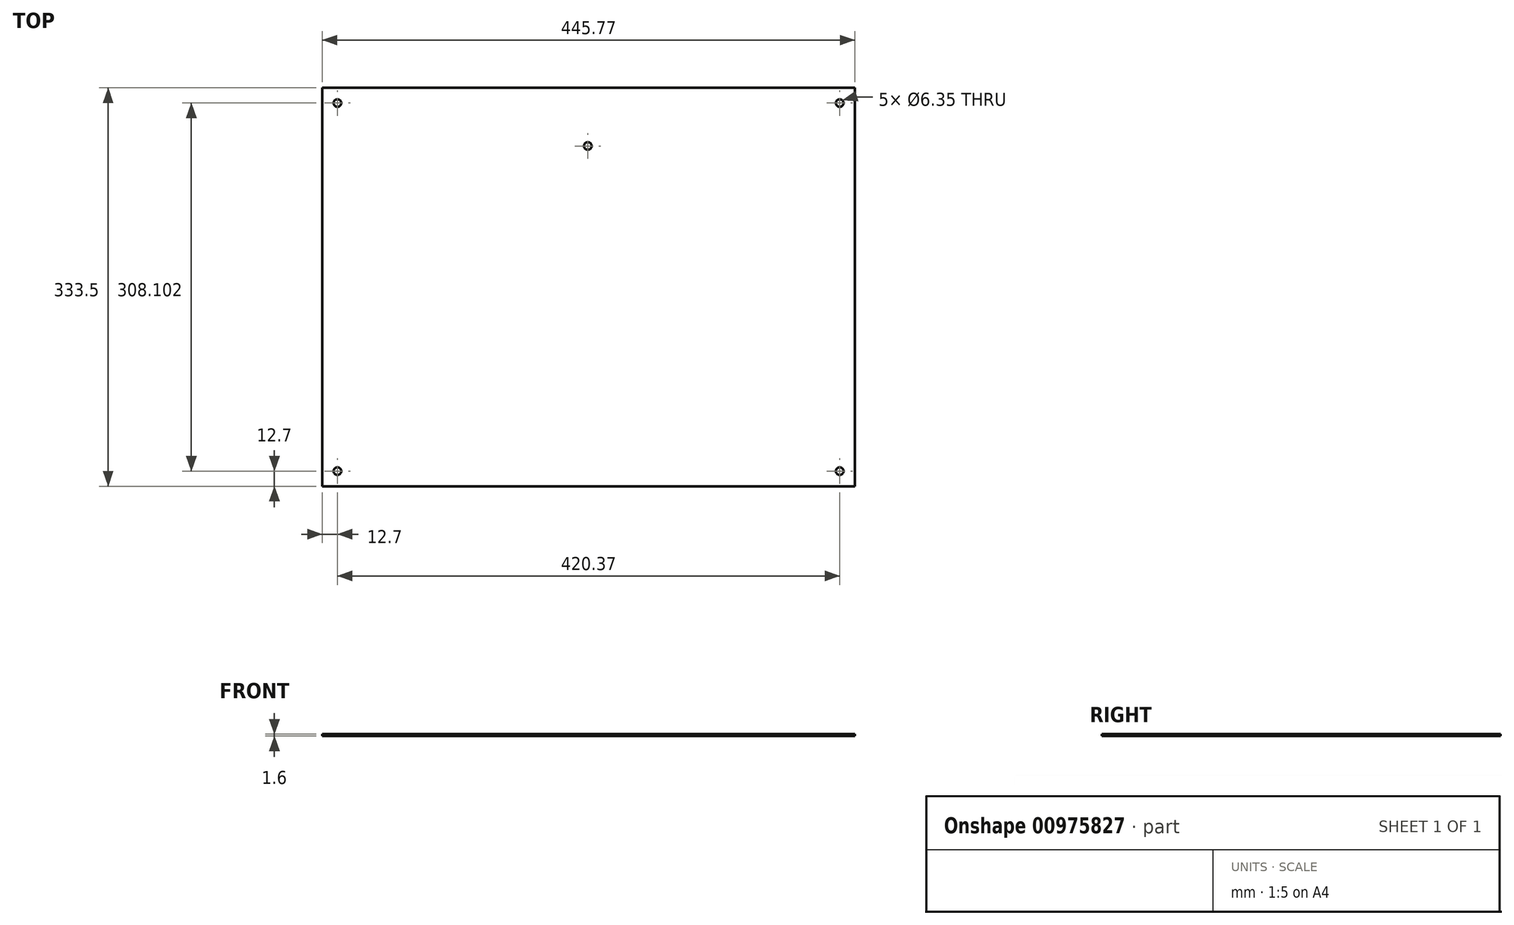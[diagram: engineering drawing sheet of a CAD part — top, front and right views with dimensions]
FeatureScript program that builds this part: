
annotation { "Feature Type Name" : "Feature", "Feature Type Description" : "" }
export const myFeature = defineFeature(function(context is Context, id is Id, definition is map)
    precondition{}
    {
        {
            var Q0;
            Q0=qCreatedBy(makeId("Top.planeOp"),FACE);
            var sketch = newSketch(context, id + "F0", { "sketchPlane" : qUnion([Q0])});
            skCircle(sketch, "E0", {"center": v(12.7, 320.8) * mm, "radius": 3.18 * mm});
            skCircle(sketch, "E1", {"center": v(433.07, 320.8) * mm, "radius": 3.18 * mm});
            skCircle(sketch, "E2", {"center": v(433.07, 12.7) * mm, "radius": 3.18 * mm});
            skCircle(sketch, "E3", {"center": v(12.7, 12.7) * mm, "radius": 3.18 * mm});
            skCircle(sketch, "E4", {"center": v(222.25, 284.86) * mm, "radius": 3.18 * mm});
            skLineSegment(sketch, "E5.bottom", {"start": v(0, 333.5) * mm, "end": v(445.77, 333.5) * mm});
            skLineSegment(sketch, "E5.top", {"start": v(0, 0) * mm, "end": v(445.77, 0) * mm});
            skLineSegment(sketch, "E5.left", {"start": v(0, 333.5) * mm, "end": v(0, 0) * mm});
            skLineSegment(sketch, "E5.right", {"start": v(445.77, 333.5) * mm, "end": v(445.77, 0) * mm});
            skSolve(sketch);
        }
        {
            var Q0;
            Q0=makeQuery(id+"F0.imprint","IMPRINT",FACE,{"disambiguationData":[TD([[makeQuery(id+"F0.imprint","IMPRINT",EDGE,{"derivedFrom":sQuery(id+"F0.wireOp",EDGE,"E0")}),-1.0]])]});
            extrude(context, id + "F1", {"entities" : qUnion([Q0]), "depth" : 1.6 * mm, "offsetDistance" : 25.4 * mm});
        }
    });
